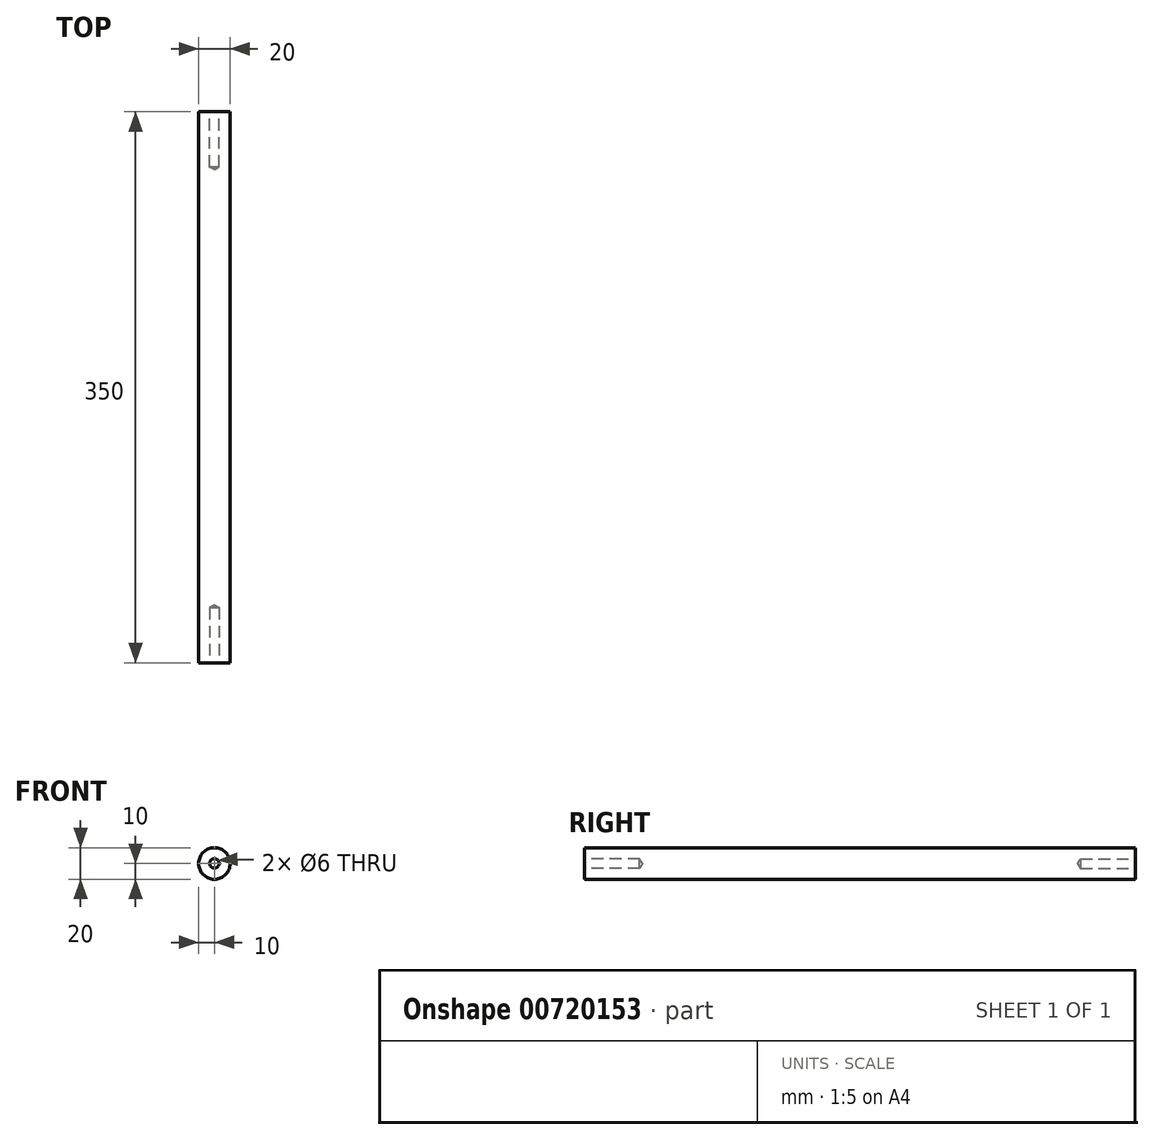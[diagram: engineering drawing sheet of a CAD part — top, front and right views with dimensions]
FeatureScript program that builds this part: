
annotation { "Feature Type Name" : "Feature", "Feature Type Description" : "" }
export const myFeature = defineFeature(function(context is Context, id is Id, definition is map)
    precondition{}
    {
        {
            var Q0;
            Q0=qCreatedBy(makeId("Front.planeOp"),FACE);
            var sketch = newSketch(context, id + "F0", { "sketchPlane" : qUnion([Q0])});
            skCircle(sketch, "E0", {"center": v(0, 0) * mm, "radius": 10 * mm});
            skSolve(sketch);
        }
        {
            var Q0;
            Q0=makeQuery(id+"F0.imprint","IMPRINT",FACE,{"disambiguationData":[TD([[makeQuery(id+"F0.imprint","IMPRINT",EDGE,{"derivedFrom":sQuery(id+"F0.wireOp",EDGE,"E0")}),1.0]])]});
            extrude(context, id + "F1", {"entities" : qUnion([Q0]), "depth" : 350 * mm, "offsetDistance" : 25 * mm});
        }
        {
            var Q0;
            Q0=makeQuery(id+"F1.opExtrude","CAP_FACE",FACE,{"disambiguationData":[OSD([sQuery(id+"F0.wireOp",EDGE,"E0")])],"isStart":false});
            var sketch = newSketch(context, id + "F2", { "sketchPlane" : qUnion([Q0])});
            skCircle(sketch, "E1", {"center": v(0, 0) * mm, "radius": 3 * mm});
            skSolve(sketch);
        }
        {
            var Q0;
            Q0=sQuery(id+"F2.wireOp",VERTEX,"E1.center");
            var Q1;
            Q1=makeQuery(id+"F1.opExtrude","SWEPT_BODY",BODY,{"disambiguationData":[OSD([sQuery(id+"F0.wireOp",EDGE,"E0")])]});
            hole(context, id + "F3", {"style" : HoleStyle.SIMPLE, "endStyle" : HoleEndStyle.BLIND, "holeDiameter" : 6 * mm, "majorDiameter" : 5 * mm, "holeDepth" : 35 * mm, "isTappedThrough" : true, "tappedDepth" : 12 * mm, "tapClearance" : 3, "startFromSketch" : true, "locations" : qUnion([Q0]), "scope" : qUnion([Q1])});
        }
        {
            var Q0;
            Q0=makeQuery(id+"F1.opExtrude","CAP_FACE",FACE,{"disambiguationData":[OSD([sQuery(id+"F0.wireOp",EDGE,"E0")])],"isStart":true});
            var sketch = newSketch(context, id + "F4", { "sketchPlane" : qUnion([Q0])});
            skPoint(sketch, "E2", {"position": v(0, 0) * mm});
            skSolve(sketch);
        }
        {
            var Q0;
            Q0=sQuery(id+"F4.wireOp",VERTEX,"E2");
            var Q1;
            Q1=makeQuery(id+"F1.opExtrude","SWEPT_BODY",BODY,{"disambiguationData":[OSD([sQuery(id+"F0.wireOp",EDGE,"E0")])]});
            hole(context, id + "F5", {"style" : HoleStyle.SIMPLE, "endStyle" : HoleEndStyle.BLIND, "holeDiameter" : 6 * mm, "majorDiameter" : 5 * mm, "holeDepth" : 35 * mm, "isTappedThrough" : true, "tappedDepth" : 12 * mm, "tapClearance" : 3, "startFromSketch" : true, "locations" : qUnion([Q0]), "scope" : qUnion([Q1])});
        }
    });
